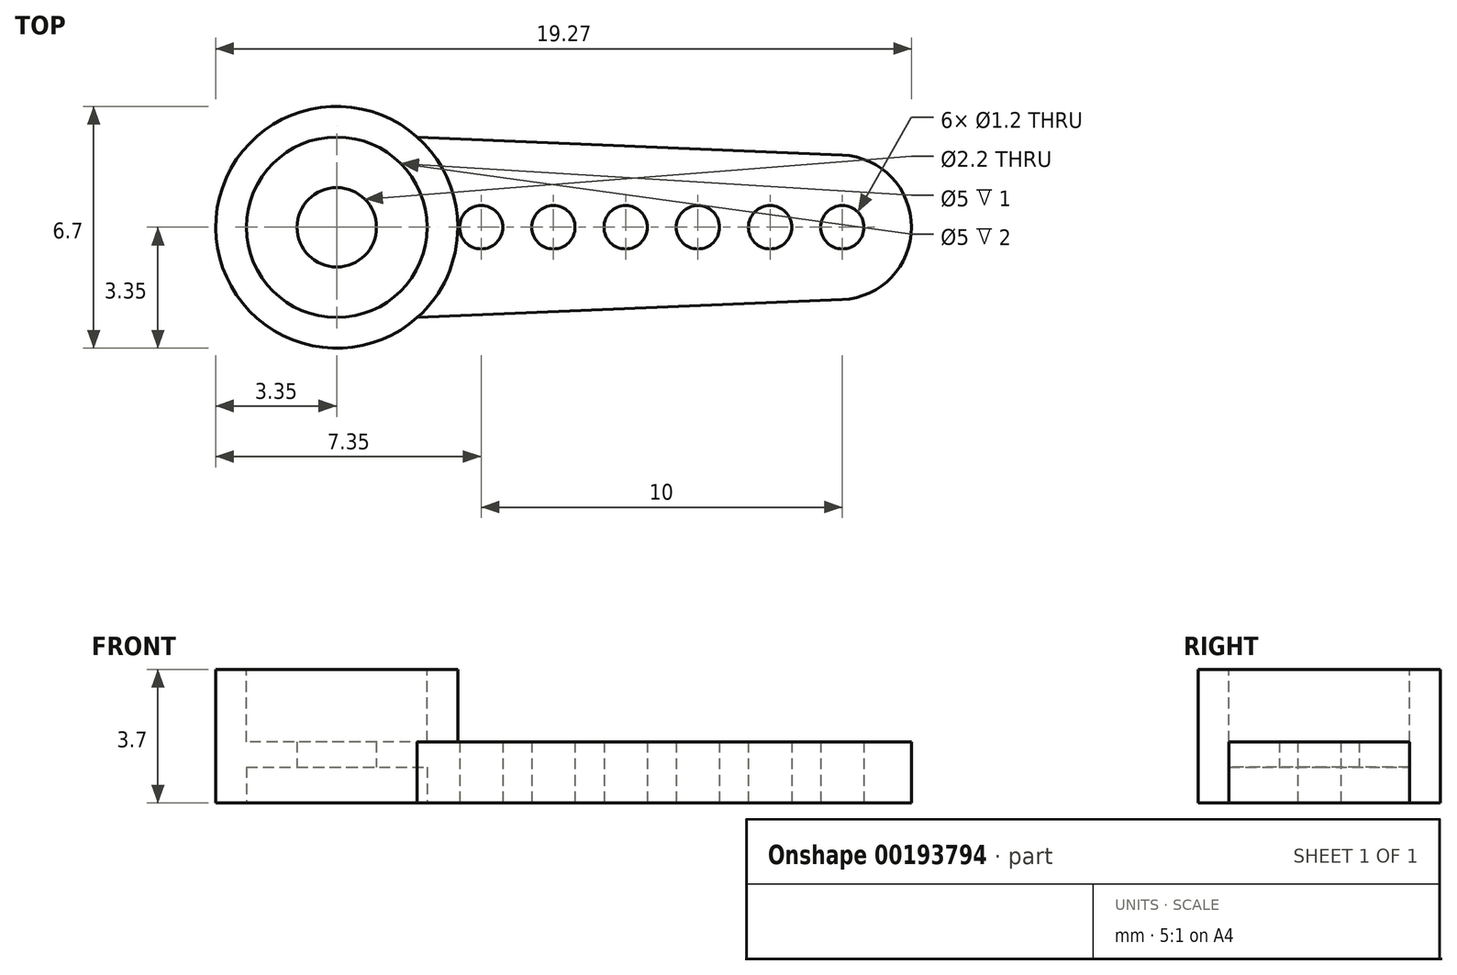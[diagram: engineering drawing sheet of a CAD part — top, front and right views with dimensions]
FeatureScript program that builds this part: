
annotation { "Feature Type Name" : "Feature", "Feature Type Description" : "" }
export const myFeature = defineFeature(function(context is Context, id is Id, definition is map)
    precondition{}
    {
        {
            var Q0;
            Q0=qCreatedBy(makeId("Top.planeOp"),FACE);
            var sketch = newSketch(context, id + "F0", { "sketchPlane" : qUnion([Q0])});
            skCircle(sketch, "E0", {"center": v(0, 0) * mm, "radius": 3.35 * mm});
            skLineSegment(sketch, "E1", {"start": v(0, 0) * mm, "end": v(-2.56, 0) * mm, "construction": true});
            skLineSegment(sketch, "E2", {"start": v(0, 0) * mm, "end": v(6, 0) * mm, "construction": true});
            skCircle(sketch, "E3", {"center": v(6, 0) * mm, "radius": 0.6 * mm});
            skCircle(sketch, "E4.1.0.0", {"center": v(8, 0) * mm, "radius": 0.6 * mm});
            skCircle(sketch, "E4.2.0.0", {"center": v(10, 0) * mm, "radius": 0.6 * mm});
            skCircle(sketch, "E4.3.0.0", {"center": v(12, 0) * mm, "radius": 0.6 * mm});
            skCircle(sketch, "E4.4.0.0", {"center": v(14, 0) * mm, "radius": 0.6 * mm});
            skLineSegment(sketch, "E4.direction1", {"start": v(6, 0) * mm, "end": v(8, 0) * mm, "construction": true});
            skCircle(sketch, "E5.1.0.0", {"center": v(4, 0) * mm, "radius": 0.6 * mm});
            skLineSegment(sketch, "E5.direction1", {"start": v(6, 0) * mm, "end": v(4, 0) * mm, "construction": true});
            skLineSegment(sketch, "E6", {"start": v(14, 2) * mm, "end": v(2.23, 2.5) * mm});
            skLineSegment(sketch, "E7.MirrorCS", {"start": v(14, -2) * mm, "end": v(2.23, -2.5) * mm});
            skArc(sketch, "E8", {"start": v(14, 2) * mm, "mid": v(15.92, 0) * mm, "end": v(14, -2) * mm});
            skLineSegment(sketch, "E9", {"start": v(0, 5) * mm, "end": v(0, -4.95) * mm, "construction": true});
            skSolve(sketch);
        }
        {
            var Q0;
            Q0 = qSketchRegion(id + "F0", true);
            extrude(context, id + "F1", {"entities" : qUnion([Q0]), "depth" : 1.7 * mm});
        }
        {
            var Q0;
            Q0=makeQuery(id+"F1.opExtrude","CAP_FACE",FACE,{"disambiguationData":[OSD([sQuery(id+"F0.wireOp",EDGE,"E0"),sQuery(id+"F0.wireOp",EDGE,"E3"),sQuery(id+"F0.wireOp",EDGE,"E4.1.0.0"),sQuery(id+"F0.wireOp",EDGE,"E4.2.0.0"),sQuery(id+"F0.wireOp",EDGE,"E4.3.0.0"),sQuery(id+"F0.wireOp",EDGE,"E4.4.0.0"),sQuery(id+"F0.wireOp",EDGE,"E5.1.0.0"),sQuery(id+"F0.wireOp",EDGE,"E6"),sQuery(id+"F0.wireOp",EDGE,"E7.MirrorCS"),sQuery(id+"F0.wireOp",EDGE,"E8")])],"isStart":false});
            var sketch = newSketch(context, id + "F2", { "sketchPlane" : qUnion([Q0])});
            skCircle(sketch, "E10", {"center": v(0, 0) * mm, "radius": 3.35 * mm});
            skPoint(sketch, "E10.first.point", {"position": v(2.23, 2.5) * mm});
            skPoint(sketch, "E10.second.point", {"position": v(2.23, -2.5) * mm});
            skPoint(sketch, "E10.third.point", {"position": v(-3.35, 0.14) * mm});
            skSolve(sketch);
        }
        {
            var Q0;
            Q0 = qSketchRegion(id + "F2", true);
            extrude(context, id + "F3", {"entities" : qUnion([Q0]), "operationType" : NewBodyOperationType.ADD, "depth" : 2 * mm});
        }
        {
            var Q0;
            Q0=makeQuery(id+"F1.opExtrude","CAP_FACE",FACE,{"disambiguationData":[OSD([sQuery(id+"F0.wireOp",EDGE,"E0"),sQuery(id+"F0.wireOp",EDGE,"E3"),sQuery(id+"F0.wireOp",EDGE,"E4.1.0.0"),sQuery(id+"F0.wireOp",EDGE,"E4.2.0.0"),sQuery(id+"F0.wireOp",EDGE,"E4.3.0.0"),sQuery(id+"F0.wireOp",EDGE,"E4.4.0.0"),sQuery(id+"F0.wireOp",EDGE,"E5.1.0.0"),sQuery(id+"F0.wireOp",EDGE,"E6"),sQuery(id+"F0.wireOp",EDGE,"E7.MirrorCS"),sQuery(id+"F0.wireOp",EDGE,"E8")])],"isStart":true});
            var sketch = newSketch(context, id + "F4", { "sketchPlane" : qUnion([Q0])});
            skCircle(sketch, "E11", {"center": v(0, 0) * mm, "radius": 2.5 * mm});
            skSolve(sketch);
        }
        {
            var Q0;
            Q0 = qSketchRegion(id + "F4", true);
            extrude(context, id + "F5", {"entities" : qUnion([Q0]), "operationType" : NewBodyOperationType.REMOVE, "oppositeDirection" : true, "depth" : 1 * mm});
        }
        {
            var Q0;
            Q0=makeQuery(id+"F5.boolean.opBoolean","COPY",FACE,{"derivedFrom":makeQuery(id+"F5.opExtrude","CAP_FACE",FACE,{"disambiguationData":[OSD([sQuery(id+"F4.wireOp",EDGE,"E11")])],"isStart":false})});
            var sketch = newSketch(context, id + "F6", { "sketchPlane" : qUnion([Q0])});
            skCircle(sketch, "E12", {"center": v(0, 0) * mm, "radius": 1.1 * mm});
            skSolve(sketch);
        }
        {
            var Q0;
            Q0 = qSketchRegion(id + "F6", true);
            extrude(context, id + "F7", {"entities" : qUnion([Q0]), "operationType" : NewBodyOperationType.REMOVE, "endBound" : BoundingType.THROUGH_ALL, "oppositeDirection" : true, "depth" : 1 * mm});
        }
        {
            var Q0;
            Q0=makeQuery(id+"F3.opExtrude","CAP_FACE",FACE,{"disambiguationData":[OSD([sQuery(id+"F2.wireOp",EDGE,"E10")])],"isStart":false});
            var sketch = newSketch(context, id + "F8", { "sketchPlane" : qUnion([Q0])});
            skCircle(sketch, "E13", {"center": v(0, 0) * mm, "radius": 2.5 * mm});
            skSolve(sketch);
        }
        {
            var Q0;
            Q0 = qSketchRegion(id + "F8", true);
            extrude(context, id + "F9", {"entities" : qUnion([Q0]), "operationType" : NewBodyOperationType.REMOVE, "oppositeDirection" : true, "depth" : 2 * mm});
        }
    });
